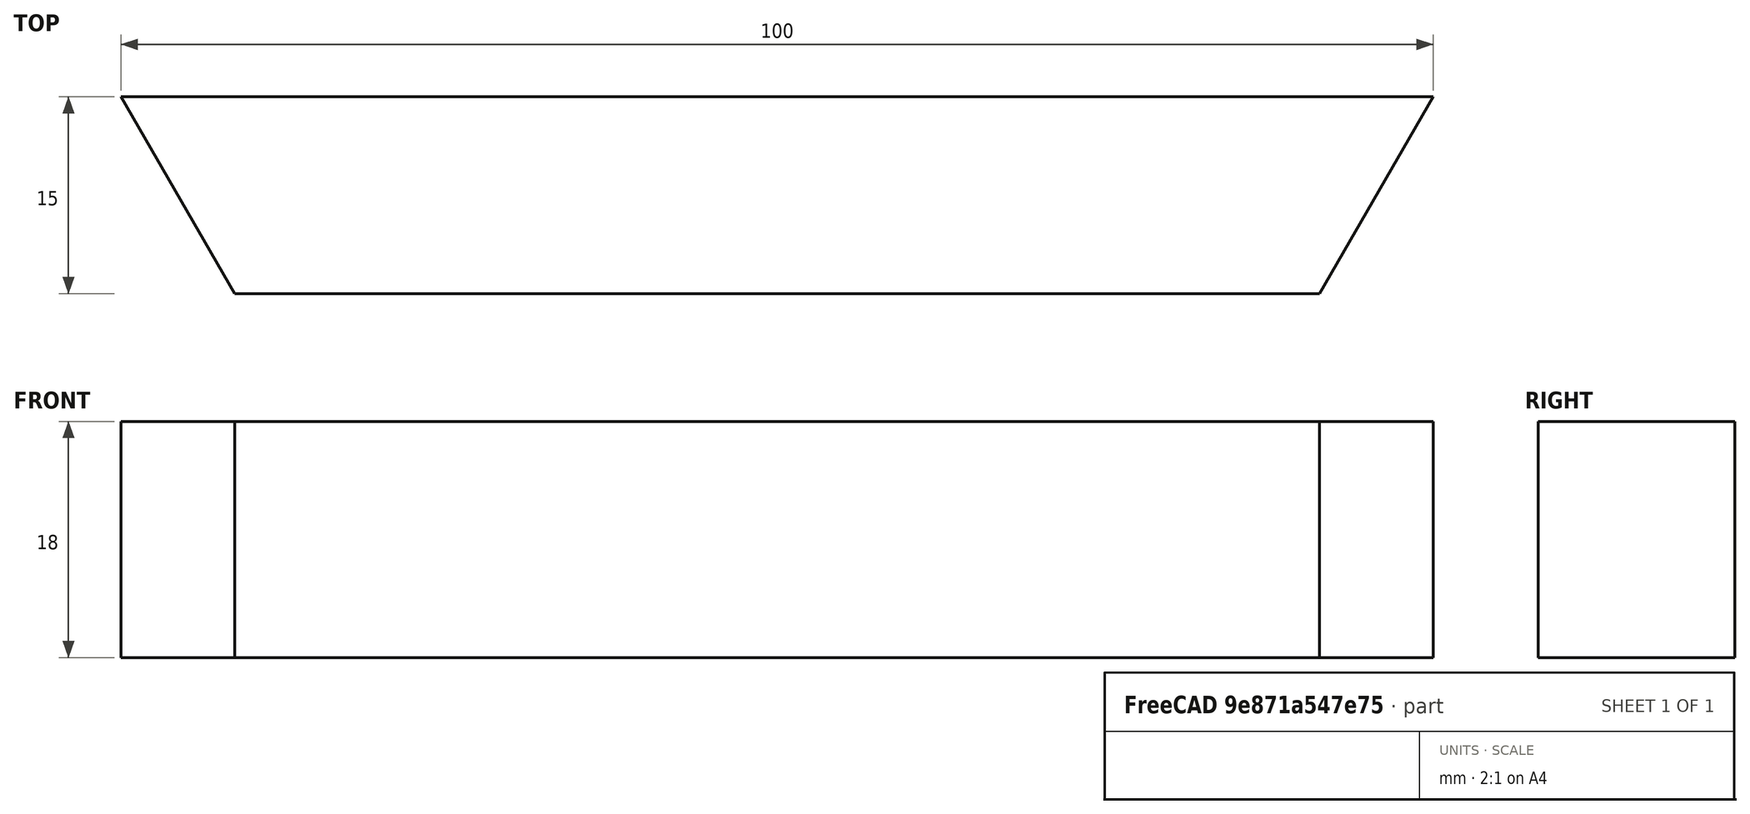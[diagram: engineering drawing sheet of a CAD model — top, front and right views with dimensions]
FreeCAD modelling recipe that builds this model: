
FCSTD DOCUMENT  (FreeCAD 0.18R4 (GitTag))
Label: Side
License: All rights reserved
LicenseURL: http://en.wikipedia.org/wiki/All_rights_reserved
objects: Sketcher::SketchObject×1, PartDesign::Pad×1, PartDesign::Body×1
note: 4 computed .brp shape members not serialized (recipe doc carries the construction recipe); baked Part::Feature solids carry a one-line shape summary decoded from their .brp

FEATURE [Sketcher::SketchObject] Sketch
  MapMode = 5
  Support = -> [XY_Plane]
  sketch-geometry (4):
    g0: LineSegment StartX=-8.66025 StartY=0 StartZ=0 EndX=-91.3397 EndY=0 EndZ=0
    g1: LineSegment StartX=-100 StartY=15 StartZ=0 EndX=0 EndY=15 EndZ=0
    g2: LineSegment StartX=-8.66025 StartY=0 StartZ=0 EndX=0 EndY=15 EndZ=0
    g3: LineSegment StartX=-91.3397 StartY=0 StartZ=0 EndX=-100 EndY=15 EndZ=0
  constraints (12):
    c: Coincident(g2,g1)
    c: Coincident(g0,g2)
    c: PointOnObject(g0,g-1)
    c: PointOnObject(g0,g-1)
    c: PointOnObject(g1,g-2)
    c: Horizontal(g1)
    c: Angle(g2,g0) = 2.0944
    c: DistanceY(g2,g2) = 15
    c: Coincident(g1,g3)
    c: Angle(g0,g3) = 2.0944
    c: Coincident(g3,g0)
    c: DistanceX(g1,g1) = 100
FEATURE [PartDesign::Pad] Pad
  Length = 18
  Length2 = 100
  Profile = -> Sketch
  Type = 0
FEATURE [PartDesign::Body] Body
  Group = -> [Sketch,Pad]
  Origin = -> Origin
  Tip = -> Pad
